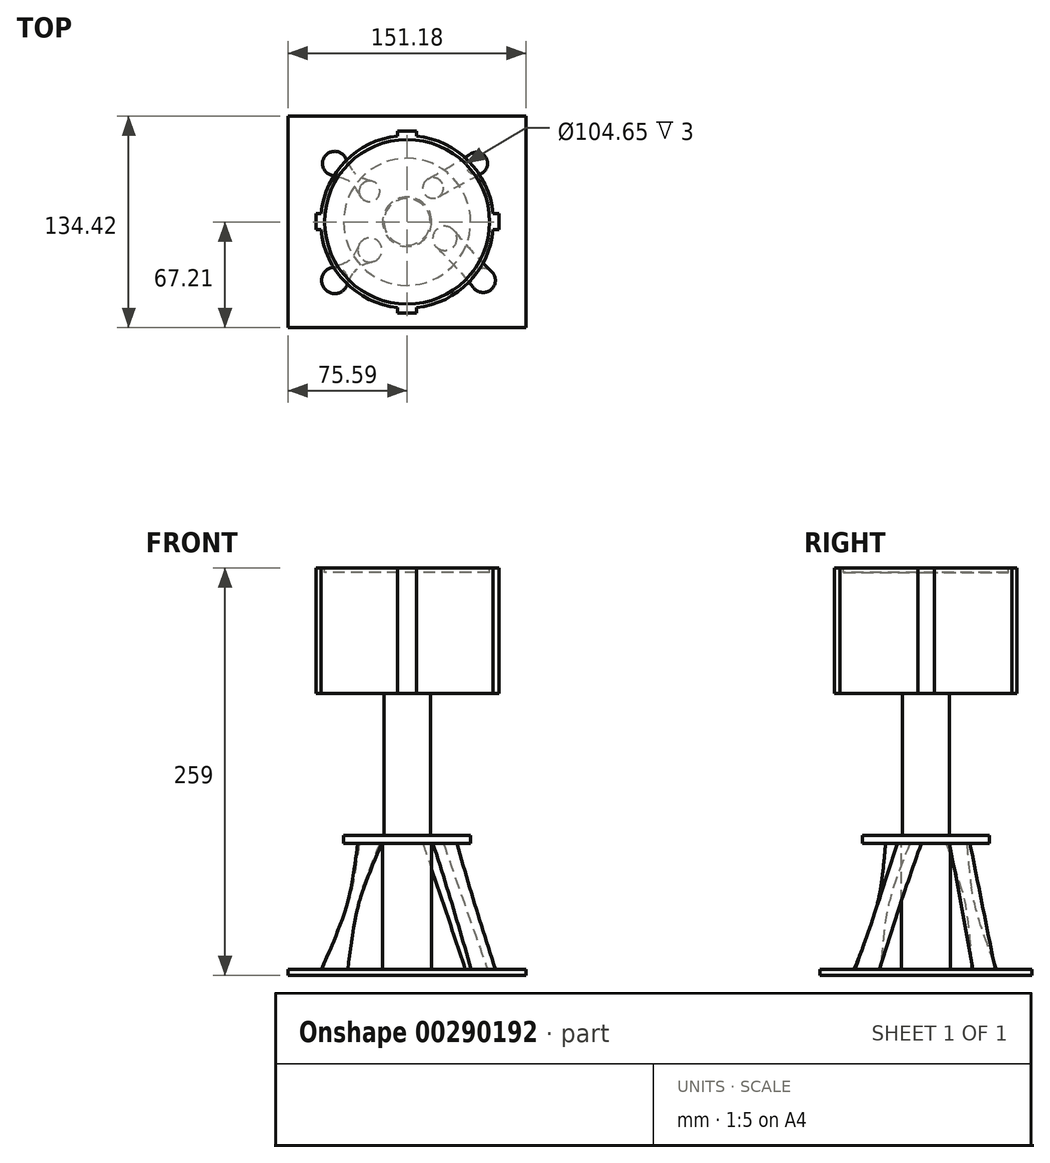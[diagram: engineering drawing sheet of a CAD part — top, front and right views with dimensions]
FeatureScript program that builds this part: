
annotation { "Feature Type Name" : "Feature", "Feature Type Description" : "" }
export const myFeature = defineFeature(function(context is Context, id is Id, definition is map)
    precondition{}
    {
        {
            var Q0;
            Q0=qCreatedBy(makeId("Top.planeOp"),FACE);
            var sketch = newSketch(context, id + "F0", { "sketchPlane" : qUnion([Q0])});
            skCircle(sketch, "E0", {"center": v(0, 0) * mm, "radius": 54.87 * mm});
            skLineSegment(sketch, "E1.bottom", {"start": v(-6.1, 49.53) * mm, "end": v(6.1, 49.53) * mm});
            skLineSegment(sketch, "E1.top", {"start": v(-6.1, 57.76) * mm, "end": v(6.1, 57.76) * mm});
            skLineSegment(sketch, "E1.left", {"start": v(-6.1, 49.53) * mm, "end": v(-6.1, 57.76) * mm});
            skLineSegment(sketch, "E1.right", {"start": v(6.1, 49.53) * mm, "end": v(6.1, 57.76) * mm});
            skLineSegment(sketch, "E2.bottom", {"start": v(47.55, 5.33) * mm, "end": v(58.22, 5.33) * mm});
            skLineSegment(sketch, "E2.top", {"start": v(47.55, -5.03) * mm, "end": v(58.22, -5.03) * mm});
            skLineSegment(sketch, "E2.left", {"start": v(47.55, 5.33) * mm, "end": v(47.55, -5.03) * mm});
            skLineSegment(sketch, "E2.right", {"start": v(58.22, 5.33) * mm, "end": v(58.22, -5.03) * mm});
            skLineSegment(sketch, "E3.bottom", {"start": v(-6.1, -49.23) * mm, "end": v(6.1, -49.23) * mm});
            skLineSegment(sketch, "E3.top", {"start": v(-6.1, -58.06) * mm, "end": v(6.1, -58.06) * mm});
            skLineSegment(sketch, "E3.left", {"start": v(-6.1, -49.23) * mm, "end": v(-6.1, -58.06) * mm});
            skLineSegment(sketch, "E3.right", {"start": v(6.1, -49.23) * mm, "end": v(6.1, -58.06) * mm});
            skLineSegment(sketch, "E4.bottom", {"start": v(-47.24, 5.33) * mm, "end": v(-57.91, 5.33) * mm});
            skLineSegment(sketch, "E4.top", {"start": v(-47.24, -5.03) * mm, "end": v(-57.91, -5.03) * mm});
            skLineSegment(sketch, "E4.left", {"start": v(-47.24, 5.33) * mm, "end": v(-47.24, -5.03) * mm});
            skLineSegment(sketch, "E4.right", {"start": v(-57.91, 5.33) * mm, "end": v(-57.91, -5.03) * mm});
            skSolve(sketch);
        }
        {
            var Q0;
            Q0 = qSketchRegion(id + "F0", true);
            extrude(context, id + "F1", {"entities" : qUnion([Q0]), "depth" : 70 * mm});
        }
        {
            var Q0;
            Q0=makeQuery(id+"F1.opExtrude","CAP_FACE",FACE,{"disambiguationData":[OSD([sQuery(id+"F0.wireOp",EDGE,"E0")])],"isStart":false});
            var sketch = newSketch(context, id + "F2", { "sketchPlane" : qUnion([Q0])});
            skCircle(sketch, "E5", {"center": v(0, 0) * mm, "radius": 52.32 * mm});
            skSolve(sketch);
        }
        {
            var Q0;
            Q0=makeQuery(id+"F2.imprint","IMPRINT",FACE,{"disambiguationData":[TD([[makeQuery(id+"F2.imprint","IMPRINT",EDGE,{"derivedFrom":sQuery(id+"F2.wireOp",EDGE,"E5")}),1.0]])]});
            extrude(context, id + "F3", {"entities" : qUnion([Q0]), "operationType" : NewBodyOperationType.REMOVE, "oppositeDirection" : true, "depth" : 3 * mm});
        }
        {
            var Q0;
            Q0 = qSketchRegion(id + "F0", true);
            extrude(context, id + "F4", {"entities" : qUnion([Q0]), "operationType" : NewBodyOperationType.ADD, "oppositeDirection" : true, "depth" : 10 * mm});
        }
        {
            var Q0;
            Q0=makeQuery(id+"F4.opExtrude","CAP_FACE",FACE,{"disambiguationData":[OSD([sQuery(id+"F0.wireOp",EDGE,"E0"),sQuery(id+"F0.wireOp",EDGE,"E1.top"),sQuery(id+"F0.wireOp",EDGE,"E1.left"),sQuery(id+"F0.wireOp",EDGE,"E1.right"),sQuery(id+"F0.wireOp",EDGE,"E2.bottom"),sQuery(id+"F0.wireOp",EDGE,"E2.top"),sQuery(id+"F0.wireOp",EDGE,"E2.right"),sQuery(id+"F0.wireOp",EDGE,"E3.top"),sQuery(id+"F0.wireOp",EDGE,"E3.left"),sQuery(id+"F0.wireOp",EDGE,"E3.right"),sQuery(id+"F0.wireOp",EDGE,"E4.bottom"),sQuery(id+"F0.wireOp",EDGE,"E4.top"),sQuery(id+"F0.wireOp",EDGE,"E4.right")])],"isStart":false});
            var sketch = newSketch(context, id + "F5", { "sketchPlane" : qUnion([Q0])});
            skCircle(sketch, "E6", {"center": v(0, 0) * mm, "radius": 14.8 * mm});
            skSolve(sketch);
        }
        {
            var Q0;
            Q0 = qSketchRegion(id + "F5", true);
            extrude(context, id + "F6", {"entities" : qUnion([Q0]), "operationType" : NewBodyOperationType.ADD, "depth" : 90 * mm});
        }
        {
            var Q0;
            Q0=makeQuery(id+"F6.opExtrude","CAP_FACE",FACE,{"disambiguationData":[OSD([sQuery(id+"F5.wireOp",EDGE,"E6")])],"isStart":false});
            var sketch = newSketch(context, id + "F7", { "sketchPlane" : qUnion([Q0])});
            skCircle(sketch, "E7", {"center": v(0, 0) * mm, "radius": 40.34 * mm});
            skSolve(sketch);
        }
        {
            var Q0;
            Q0 = qSketchRegion(id + "F7", true);
            extrude(context, id + "F8", {"entities" : qUnion([Q0]), "operationType" : NewBodyOperationType.ADD, "depth" : 5 * mm});
        }
        {
            var Q0;
            Q0=makeQuery(id+"F8.opExtrude","CAP_FACE",FACE,{"disambiguationData":[OSD([sQuery(id+"F7.wireOp",EDGE,"E7")])],"isStart":false});
            var sketch = newSketch(context, id + "F9", { "sketchPlane" : qUnion([Q0])});
            skCircle(sketch, "E8", {"center": v(0, 0) * mm, "radius": 15.64 * mm});
            skSolve(sketch);
        }
        {
            var Q0;
            Q0 = qSketchRegion(id + "F9", true);
            extrude(context, id + "F10", {"entities" : qUnion([Q0]), "operationType" : NewBodyOperationType.ADD, "depth" : 80 * mm});
        }
        {
            var Q0;
            Q0=makeQuery(id+"F10.opExtrude","CAP_FACE",FACE,{"disambiguationData":[OSD([sQuery(id+"F9.wireOp",EDGE,"E8")])],"isStart":false});
            var sketch = newSketch(context, id + "F11", { "sketchPlane" : qUnion([Q0])});
            skLineSegment(sketch, "E9.bottom", {"start": v(75.6, 67.2) * mm, "end": v(-75.6, 67.2) * mm});
            skLineSegment(sketch, "E9.top", {"start": v(75.6, -67.2) * mm, "end": v(-75.6, -67.2) * mm});
            skLineSegment(sketch, "E9.left", {"start": v(75.6, 67.2) * mm, "end": v(75.6, -67.2) * mm});
            skLineSegment(sketch, "E9.right", {"start": v(-75.6, 67.2) * mm, "end": v(-75.6, -67.2) * mm});
            skPoint(sketch, "E9.middle", {"position": v(0, 0) * mm});
            skSolve(sketch);
        }
        {
            var Q0;
            Q0 = qSketchRegion(id + "F11", true);
            extrude(context, id + "F12", {"entities" : qUnion([Q0]), "operationType" : NewBodyOperationType.ADD, "depth" : 4 * mm});
        }
        {
            var Q0;
            Q0=makeQuery(id+"F12.opExtrude","CAP_FACE",FACE,{"disambiguationData":[OSD([sQuery(id+"F11.wireOp",EDGE,"E9.bottom"),sQuery(id+"F11.wireOp",EDGE,"E9.top"),sQuery(id+"F11.wireOp",EDGE,"E9.left"),sQuery(id+"F11.wireOp",EDGE,"E9.right")])],"isStart":true});
            var sketch = newSketch(context, id + "F13", { "sketchPlane" : qUnion([Q0])});
            skCircle(sketch, "E10", {"center": v(44.03, 37.06) * mm, "radius": 7.1 * mm});
            skCircle(sketch, "E11", {"center": v(-45.96, 37.06) * mm, "radius": 7.71 * mm});
            skCircle(sketch, "E12", {"center": v(-45.96, -37.22) * mm, "radius": 8.34 * mm});
            skCircle(sketch, "E13", {"center": v(48.37, -37.22) * mm, "radius": 7.68 * mm});
            skSolve(sketch);
        }
        {
            var Q0;
            Q0=makeQuery(id+"F8.opExtrude","CAP_FACE",FACE,{"disambiguationData":[OSD([sQuery(id+"F7.wireOp",EDGE,"E7")])],"isStart":false});
            var sketch = newSketch(context, id + "F14", { "sketchPlane" : qUnion([Q0])});
            skCircle(sketch, "E14", {"center": v(23.97, 10.5) * mm, "radius": 7.68 * mm});
            skCircle(sketch, "E15", {"center": v(-23.64, 17.88) * mm, "radius": 7.68 * mm});
            skCircle(sketch, "E16", {"center": v(-23.87, -19.38) * mm, "radius": 6.56 * mm});
            skCircle(sketch, "E17", {"center": v(16.49, -21.5) * mm, "radius": 6.57 * mm});
            skSolve(sketch);
        }
        {
            var Q1;
            Q1=makeQuery(id+"F13.imprint","IMPRINT",FACE,{"disambiguationData":[TD([[makeQuery(id+"F13.imprint","IMPRINT",EDGE,{"derivedFrom":sQuery(id+"F13.wireOp",EDGE,"E13")}),1.0]])]});
            var Q2;
            Q2=makeQuery(id+"F14.imprint","IMPRINT",FACE,{"disambiguationData":[TD([[makeQuery(id+"F14.imprint","IMPRINT",EDGE,{"derivedFrom":sQuery(id+"F14.wireOp",EDGE,"E14")}),1.0]])]});
            loft(context, id + "F15", {"operationType" : NewBodyOperationType.ADD, "sheetProfilesArray" : [{ "sheetProfileEntities" : qUnion([Q1]) }, { "sheetProfileEntities" : qUnion([Q2]) }]});
        }
        {
            var Q1;
            Q1=makeQuery(id+"F13.imprint","IMPRINT",FACE,{"disambiguationData":[TD([[makeQuery(id+"F13.imprint","IMPRINT",EDGE,{"derivedFrom":sQuery(id+"F13.wireOp",EDGE,"E12")}),1.0]])]});
            var Q2;
            Q2=makeQuery(id+"F14.imprint","IMPRINT",FACE,{"disambiguationData":[TD([[makeQuery(id+"F14.imprint","IMPRINT",EDGE,{"derivedFrom":sQuery(id+"F14.wireOp",EDGE,"E15")}),1.0]])]});
            loft(context, id + "F16", {"operationType" : NewBodyOperationType.ADD, "sheetProfilesArray" : [{ "sheetProfileEntities" : qUnion([Q1]) }, { "sheetProfileEntities" : qUnion([Q2]) }]});
        }
        {
            var Q1;
            Q1=makeQuery(id+"F13.imprint","IMPRINT",FACE,{"disambiguationData":[TD([[makeQuery(id+"F13.imprint","IMPRINT",EDGE,{"derivedFrom":sQuery(id+"F13.wireOp",EDGE,"E11")}),1.0]])]});
            var Q2;
            Q2=makeQuery(id+"F14.imprint","IMPRINT",FACE,{"disambiguationData":[TD([[makeQuery(id+"F14.imprint","IMPRINT",EDGE,{"derivedFrom":sQuery(id+"F14.wireOp",EDGE,"E16")}),1.0]])]});
            loft(context, id + "F17", {"operationType" : NewBodyOperationType.ADD, "sheetProfilesArray" : [{ "sheetProfileEntities" : qUnion([Q1]) }, { "sheetProfileEntities" : qUnion([Q2]) }]});
        }
        {
            var Q1;
            Q1=makeQuery(id+"F13.imprint","IMPRINT",FACE,{"disambiguationData":[TD([[makeQuery(id+"F13.imprint","IMPRINT",EDGE,{"derivedFrom":sQuery(id+"F13.wireOp",EDGE,"E10")}),1.0]])]});
            var Q2;
            Q2=makeQuery(id+"F14.imprint","IMPRINT",FACE,{"disambiguationData":[TD([[makeQuery(id+"F14.imprint","IMPRINT",EDGE,{"derivedFrom":sQuery(id+"F14.wireOp",EDGE,"E17")}),1.0]])]});
            loft(context, id + "F18", {"operationType" : NewBodyOperationType.ADD, "sheetProfilesArray" : [{ "sheetProfileEntities" : qUnion([Q1]) }, { "sheetProfileEntities" : qUnion([Q2]) }]});
        }
    });
